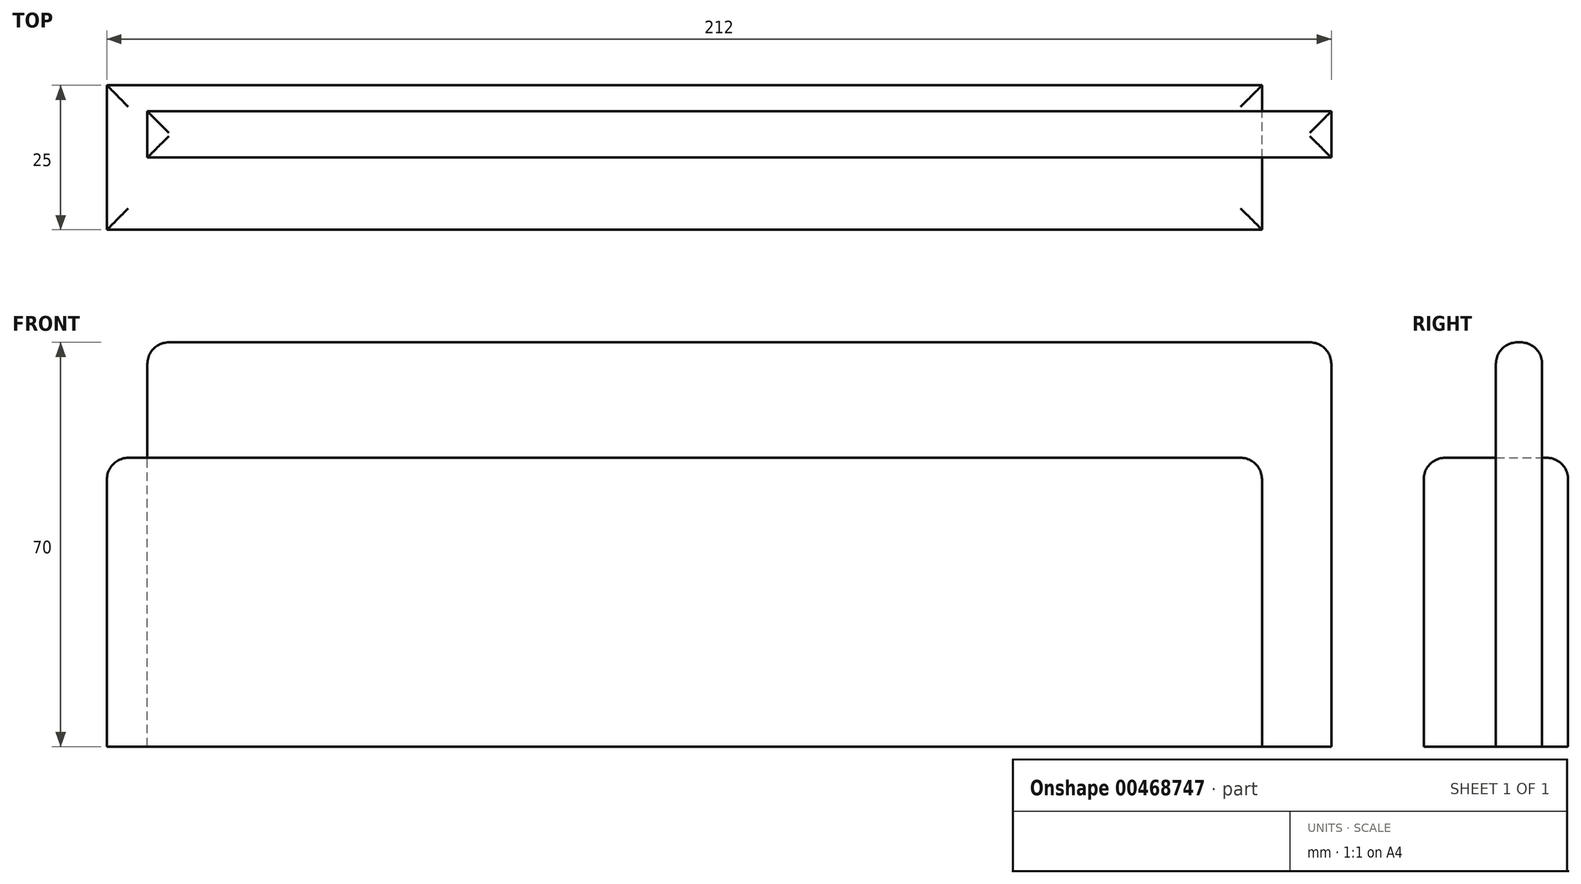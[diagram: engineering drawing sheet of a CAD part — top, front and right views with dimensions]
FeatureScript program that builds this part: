
annotation { "Feature Type Name" : "Feature", "Feature Type Description" : "" }
export const myFeature = defineFeature(function(context is Context, id is Id, definition is map)
    precondition{}
    {
        {
            var Q0;
            Q0=qCreatedBy(makeId("Front.planeOp"),FACE);
            var sketch = newSketch(context, id + "F0", { "sketchPlane" : qUnion([Q0])});
            skLineSegment(sketch, "E0.bottom", {"start": v(100, 25) * mm, "end": v(-100, 25) * mm});
            skLineSegment(sketch, "E0.top", {"start": v(100, -25) * mm, "end": v(-100, -25) * mm});
            skLineSegment(sketch, "E0.left", {"start": v(100, 25) * mm, "end": v(100, -25) * mm});
            skLineSegment(sketch, "E0.right", {"start": v(-100, 25) * mm, "end": v(-100, -25) * mm});
            skPoint(sketch, "E0.middle", {"position": v(0, 0) * mm});
            skSolve(sketch);
        }
        {
            var Q0;
            Q0=qSketchRegion(id+"F0",true);
            extrude(context, id + "F1", {"entities" : qUnion([Q0]), "endBound" : BoundingType.SYMMETRIC, "depth" : 25 * mm});
        }
        {
            var Q0;
            Q0=qCreatedBy(makeId("Front.planeOp"),FACE);
            var sketch = newSketch(context, id + "F2", { "sketchPlane" : qUnion([Q0])});
            skLineSegment(sketch, "E1.0.0", {"start": v(-100, -25) * mm, "end": v(100, -25) * mm, "construction": true});
            skLineSegment(sketch, "E1.0.1", {"start": v(100, -25) * mm, "end": v(100, 25) * mm, "construction": true});
            skLineSegment(sketch, "E1.0.2", {"start": v(100, 25) * mm, "end": v(-100, 25) * mm, "construction": true});
            skLineSegment(sketch, "E1.0.3", {"start": v(-100, 25) * mm, "end": v(-100, -25) * mm, "construction": true});
            skLineSegment(sketch, "E2.bottom", {"start": v(-93, -25) * mm, "end": v(112, -25) * mm});
            skLineSegment(sketch, "E2.top", {"start": v(-93, 45) * mm, "end": v(112, 45) * mm});
            skLineSegment(sketch, "E2.left", {"start": v(-93, -25) * mm, "end": v(-93, 45) * mm});
            skLineSegment(sketch, "E2.right", {"start": v(112, -25) * mm, "end": v(112, 45) * mm});
            skSolve(sketch);
        }
        {
            var Q0;
            Q0=qSketchRegion(id+"F2",true);
            extrude(context, id + "F3", {"entities" : qUnion([Q0]), "oppositeDirection" : true, "depth" : 8 * mm});
        }
        {
            var Q0;
            Q0=makeQuery(id+"F3.opExtrude","SWEPT_FACE",FACE,{"disambiguationData":[OSD([sQuery(id+"F2.wireOp",EDGE,"E2.top")])]});
            var Q1;
            Q1=makeQuery(id+"F1.opExtrude","SWEPT_FACE",FACE,{"disambiguationData":[OSD([sQuery(id+"F0.wireOp",EDGE,"E0.bottom")])]});
            fillet(context, id + "F4", {"entities" : qUnion([Q0, Q1]), "radius" : 3.7 * mm, "tangentPropagation" : true, "allowEdgeOverflow" : false});
        }
    });
